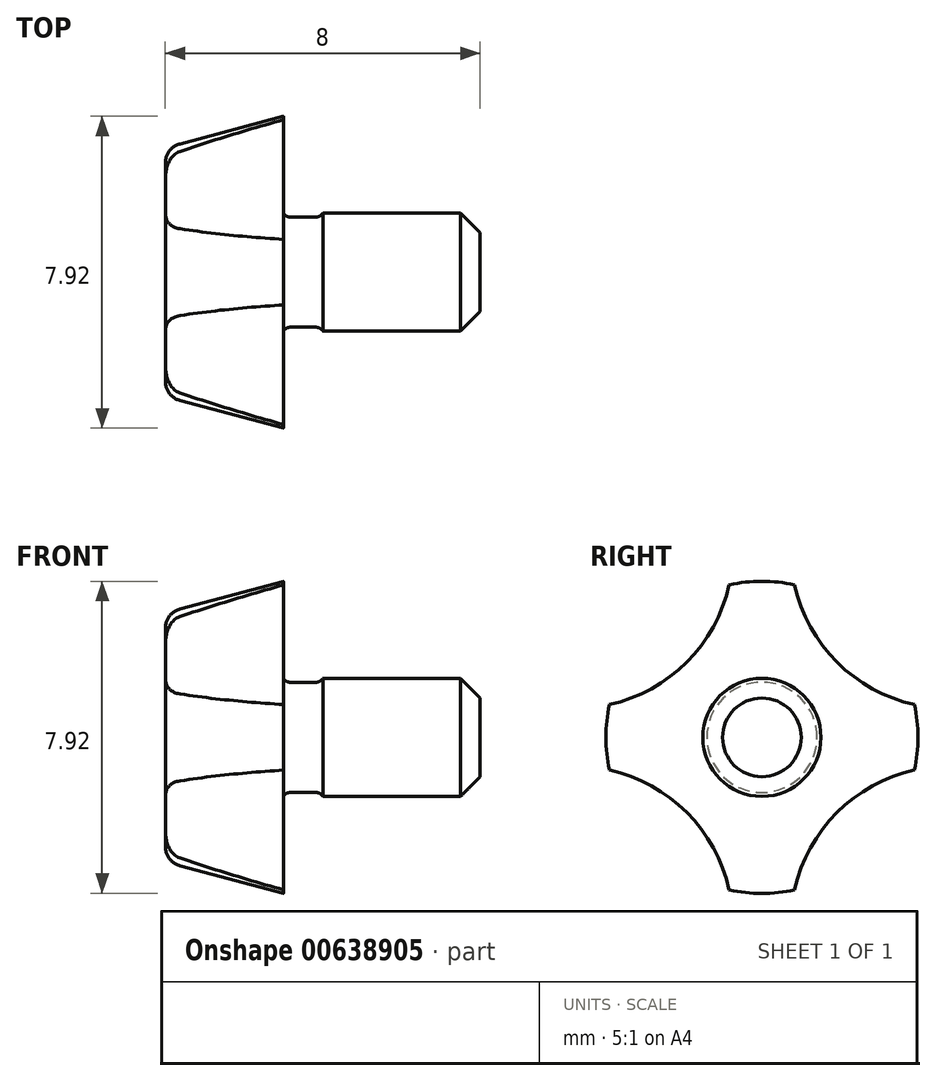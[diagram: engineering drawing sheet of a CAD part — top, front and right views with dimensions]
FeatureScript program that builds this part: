
annotation { "Feature Type Name" : "Feature", "Feature Type Description" : "" }
export const myFeature = defineFeature(function(context is Context, id is Id, definition is map)
    precondition{}
    {
        {
            var Q0;
            Q0=qCreatedBy(makeId("Front.planeOp"),FACE);
            var sketch = newSketch(context, id + "F0", { "sketchPlane" : qUnion([Q0])});
            skArc(sketch, "E0", {"start": v(6.56, 3.26) * mm, "mid": v(6.3, 3.08) * mm, "end": v(6.2, 2.78) * mm});
            skArc(sketch, "E1", {"start": v(6.2, -2.78) * mm, "mid": v(6.3, -3.08) * mm, "end": v(6.56, -3.26) * mm});
            skLineSegment(sketch, "E2", {"start": v(14.54, 0) * mm, "end": v(6.2, 0) * mm});
            skLineSegment(sketch, "E3", {"start": v(9.2, -3.96) * mm, "end": v(9.2, 3.96) * mm});
            skLineSegment(sketch, "E4", {"start": v(6.2, 2.78) * mm, "end": v(6.2, -2.78) * mm});
            skLineSegment(sketch, "E5", {"start": v(6.56, 3.26) * mm, "end": v(9.2, 3.96) * mm});
            skLineSegment(sketch, "E6", {"start": v(6.56, -3.26) * mm, "end": v(9.2, -3.96) * mm});
            skLineSegment(sketch, "E7", {"start": v(9.37, -1.4) * mm, "end": v(9.37, 1.4) * mm});
            skArc(sketch, "E8", {"start": v(9.37, -1.4) * mm, "mid": v(9.27, -1.43) * mm, "end": v(9.2, -1.5) * mm});
            skArc(sketch, "E9", {"start": v(9.2, 1.5) * mm, "mid": v(9.27, 1.43) * mm, "end": v(9.37, 1.4) * mm});
            skLineSegment(sketch, "E10", {"start": v(13.7, -1.5) * mm, "end": v(13.7, 1.5) * mm});
            skLineSegment(sketch, "E11", {"start": v(10.2, -1.5) * mm, "end": v(10.2, 1.5) * mm});
            skLineSegment(sketch, "E12", {"start": v(10.2, -1.5) * mm, "end": v(13.7, -1.5) * mm});
            skLineSegment(sketch, "E13", {"start": v(13.7, 1.5) * mm, "end": v(10.2, 1.5) * mm});
            skLineSegment(sketch, "E14", {"start": v(14.2, -1) * mm, "end": v(14.2, 1) * mm});
            skLineSegment(sketch, "E15", {"start": v(13.7, -1.5) * mm, "end": v(14.2, -1) * mm});
            skLineSegment(sketch, "E16", {"start": v(14.2, 1) * mm, "end": v(13.7, 1.5) * mm});
            skLineSegment(sketch, "E17", {"start": v(10.02, -1.4) * mm, "end": v(10.02, 1.4) * mm});
            skArc(sketch, "E18", {"start": v(10.2, -1.5) * mm, "mid": v(10.12, -1.43) * mm, "end": v(10.02, -1.4) * mm});
            skArc(sketch, "E19", {"start": v(10.02, 1.4) * mm, "mid": v(10.12, 1.43) * mm, "end": v(10.2, 1.5) * mm});
            skLineSegment(sketch, "E20", {"start": v(9.37, -1.4) * mm, "end": v(10.02, -1.4) * mm});
            skLineSegment(sketch, "E21", {"start": v(10.02, 1.4) * mm, "end": v(9.37, 1.4) * mm});
            skCircle(sketch, "E22", {"center": v(-10.58, 0) * mm, "radius": 1.5 * mm});
            skArc(sketch, "E23", {"start": v(-9.75, 3.88) * mm, "mid": v(-10.58, 3.96) * mm, "end": v(-11.41, 3.88) * mm});
            skArc(sketch, "E24", {"start": v(-6.7, -0.83) * mm, "mid": v(-6.62, 0) * mm, "end": v(-6.7, 0.83) * mm});
            skArc(sketch, "E25", {"start": v(-11.41, -3.88) * mm, "mid": v(-10.58, -3.96) * mm, "end": v(-9.75, -3.88) * mm});
            skArc(sketch, "E26", {"start": v(-14.46, 0.83) * mm, "mid": v(-14.54, 0) * mm, "end": v(-14.46, -0.83) * mm});
            skArc(sketch, "E27", {"start": v(-13.52, 1.17) * mm, "mid": v(-13.74, 0) * mm, "end": v(-13.52, -1.17) * mm});
            skArc(sketch, "E28", {"start": v(-11.75, -2.94) * mm, "mid": v(-10.58, -3.16) * mm, "end": v(-9.41, -2.94) * mm});
            skArc(sketch, "E29", {"start": v(-7.64, -1.17) * mm, "mid": v(-7.42, 0) * mm, "end": v(-7.64, 1.17) * mm});
            skArc(sketch, "E30", {"start": v(-9.41, 2.94) * mm, "mid": v(-10.58, 3.16) * mm, "end": v(-11.75, 2.94) * mm});
            skArc(sketch, "E31", {"start": v(-9.75, 3.88) * mm, "mid": v(-8.67, 1.91) * mm, "end": v(-6.7, 0.83) * mm});
            skArc(sketch, "E32", {"start": v(-6.7, -0.83) * mm, "mid": v(-8.67, -1.91) * mm, "end": v(-9.75, -3.88) * mm});
            skArc(sketch, "E33", {"start": v(-11.41, -3.88) * mm, "mid": v(-12.49, -1.91) * mm, "end": v(-14.46, -0.83) * mm});
            skArc(sketch, "E34", {"start": v(-14.46, 0.83) * mm, "mid": v(-12.49, 1.91) * mm, "end": v(-11.41, 3.88) * mm});
            skCircle(sketch, "E35", {"center": v(-10.58, 0) * mm, "radius": 3.96 * mm});
            skSolve(sketch);
        }
        {
            var Q0;
            {var subQ5=sQuery(id+"F0.wireOp",EDGE,"E9");Q0=makeQuery(id+"F0.imprint","IMPRINT",FACE,{"disambiguationData":[TD([[makeQuery(id+"F0.imprint","IMPRINT",EDGE,{"derivedFrom":subQ5}),-1.0]])]});}
            var Q1;
            {var subQ5=sQuery(id+"F0.wireOp",EDGE,"E21");Q1=makeQuery(id+"F0.imprint","IMPRINT",FACE,{"disambiguationData":[TD([[makeQuery(id+"F0.imprint","IMPRINT",EDGE,{"derivedFrom":subQ5}),1.0]])]});}
            var Q2;
            {var subQ5=sQuery(id+"F0.wireOp",EDGE,"E19");Q2=makeQuery(id+"F0.imprint","IMPRINT",FACE,{"disambiguationData":[TD([[makeQuery(id+"F0.imprint","IMPRINT",EDGE,{"derivedFrom":subQ5}),-1.0]])]});}
            var Q3;
            {var subQ5=sQuery(id+"F0.wireOp",EDGE,"E13");Q3=makeQuery(id+"F0.imprint","IMPRINT",FACE,{"disambiguationData":[TD([[makeQuery(id+"F0.imprint","IMPRINT",EDGE,{"derivedFrom":subQ5}),1.0]])]});}
            var Q4;
            {var subQ5=sQuery(id+"F0.wireOp",EDGE,"E16");Q4=makeQuery(id+"F0.imprint","IMPRINT",FACE,{"disambiguationData":[TD([[makeQuery(id+"F0.imprint","IMPRINT",EDGE,{"derivedFrom":subQ5}),1.0]])]});}
            var Q5;
            {var subQ3=sQuery(id+"F0.wireOp",EDGE,"E0");Q5=makeQuery(id+"F0.imprint","IMPRINT",FACE,{"disambiguationData":[TD([[makeQuery(id+"F0.imprint","IMPRINT",EDGE,{"derivedFrom":subQ3}),1.0]])]});}
            var Q6;
            Q6=sQuery(id+"F0.wireOp",EDGE,"E2");
            revolve(context, id + "F1", {"entities" : qUnion([Q0, Q1, Q2, Q3, Q4, Q5]), "axis" : qUnion([Q6]), "revolveType" : RevolveType.FULL});
        }
        {
            var Q0;
            Q0=makeQuery(id+"F1.opRevolve","SWEPT_FACE",FACE,{"disambiguationData":[OSD([sQuery(id+"F0.wireOp",EDGE,"E4")])]});
            var sketch = newSketch(context, id + "F2", { "sketchPlane" : qUnion([Q0])});
            skPoint(sketch, "E36", {"position": v(0, 0) * mm});
            skCircle(sketch, "E37", {"center": v(0, 0) * mm, "radius": 1.5 * mm});
            skArc(sketch, "E38", {"start": v(0.83, 3.88) * mm, "mid": v(0, 3.96) * mm, "end": v(-0.83, 3.88) * mm});
            skArc(sketch, "E39", {"start": v(3.88, -0.83) * mm, "mid": v(3.96, 0) * mm, "end": v(3.88, 0.83) * mm});
            skArc(sketch, "E40", {"start": v(-0.83, -3.88) * mm, "mid": v(0, -3.96) * mm, "end": v(0.83, -3.88) * mm});
            skArc(sketch, "E41", {"start": v(-3.88, 0.83) * mm, "mid": v(-3.96, 0) * mm, "end": v(-3.88, -0.83) * mm});
            skArc(sketch, "E42", {"start": v(-2.94, 1.17) * mm, "mid": v(-3.16, 0) * mm, "end": v(-2.94, -1.17) * mm});
            skArc(sketch, "E43", {"start": v(-1.17, -2.94) * mm, "mid": v(0, -3.16) * mm, "end": v(1.17, -2.94) * mm});
            skArc(sketch, "E44", {"start": v(2.94, -1.17) * mm, "mid": v(3.16, 0) * mm, "end": v(2.94, 1.17) * mm});
            skArc(sketch, "E45", {"start": v(1.17, 2.94) * mm, "mid": v(0, 3.16) * mm, "end": v(-1.17, 2.94) * mm});
            skArc(sketch, "E46", {"start": v(0.83, 3.88) * mm, "mid": v(1.91, 1.91) * mm, "end": v(3.88, 0.83) * mm});
            skArc(sketch, "E47", {"start": v(3.88, -0.83) * mm, "mid": v(1.91, -1.91) * mm, "end": v(0.83, -3.88) * mm});
            skArc(sketch, "E48", {"start": v(-0.83, -3.88) * mm, "mid": v(-1.91, -1.91) * mm, "end": v(-3.88, -0.83) * mm});
            skArc(sketch, "E49", {"start": v(-3.88, 0.83) * mm, "mid": v(-1.91, 1.91) * mm, "end": v(-0.83, 3.88) * mm});
            skCircle(sketch, "E50", {"center": v(0, 0) * mm, "radius": 3.96 * mm});
            skSolve(sketch);
        }
        {
            var Q0;
            {var subQ0=sQuery(id+"F2.wireOp",EDGE,"E47");var subQ8=makeQuery(id+"F2.imprint","INTERSECT",VERTEX,{"derivedFrom":[sQuery(id+"F2.wireOp",EDGE,"E43"),subQ0]});Q0=makeQuery(id+"F2.imprint","IMPRINT",FACE,{"disambiguationData":[TD([[makeQuery(id+"F2.imprint","IMPRINT",EDGE,{"disambiguationData":[TD([[subQ8,-1.0]])],"derivedFrom":subQ0}),1.0]])]});}
            var Q1;
            {var subQ0=sQuery(id+"F2.wireOp",EDGE,"E47");var subQ1=makeQuery(id+"F1.opRevolve","SWEPT_EDGE",EDGE,{"disambiguationData":[OSD([sQuery(id+"F0.wireOp",EDGE,"E0"),sQuery(id+"F0.wireOp",EDGE,"E4")])]});var subQ2=makeQuery(id+"F2.imprint","INTERSECT",VERTEX,{"disambiguationData":[OD(0.0)],"derivedFrom":[subQ1,subQ0]});Q1=makeQuery(id+"F2.imprint","IMPRINT",FACE,{"disambiguationData":[TD([[makeQuery(id+"F2.imprint","IMPRINT",EDGE,{"disambiguationData":[TD([[subQ2,-1.0]])],"derivedFrom":subQ0}),1.0]])]});}
            var Q2;
            {var subQ0=sQuery(id+"F2.wireOp",EDGE,"E48");var subQ4=makeQuery(id+"F2.imprint","INTERSECT",VERTEX,{"derivedFrom":[sQuery(id+"F2.wireOp",EDGE,"E42"),subQ0]});Q2=makeQuery(id+"F2.imprint","IMPRINT",FACE,{"disambiguationData":[TD([[makeQuery(id+"F2.imprint","IMPRINT",EDGE,{"disambiguationData":[TD([[subQ4,-1.0]])],"derivedFrom":subQ0}),1.0]])]});}
            var Q3;
            {var subQ0=sQuery(id+"F2.wireOp",EDGE,"E48");var subQ1=makeQuery(id+"F1.opRevolve","SWEPT_EDGE",EDGE,{"disambiguationData":[OSD([sQuery(id+"F0.wireOp",EDGE,"E0"),sQuery(id+"F0.wireOp",EDGE,"E4")])]});var subQ2=makeQuery(id+"F2.imprint","INTERSECT",VERTEX,{"disambiguationData":[OD(0.0)],"derivedFrom":[subQ1,subQ0]});Q3=makeQuery(id+"F2.imprint","IMPRINT",FACE,{"disambiguationData":[TD([[makeQuery(id+"F2.imprint","IMPRINT",EDGE,{"disambiguationData":[TD([[subQ2,-1.0]])],"derivedFrom":subQ0}),1.0]])]});}
            var Q4;
            {var subQ0=sQuery(id+"F2.wireOp",EDGE,"E49");var subQ1=makeQuery(id+"F1.opRevolve","SWEPT_EDGE",EDGE,{"disambiguationData":[OSD([sQuery(id+"F0.wireOp",EDGE,"E0"),sQuery(id+"F0.wireOp",EDGE,"E4")])]});var subQ2=makeQuery(id+"F2.imprint","INTERSECT",VERTEX,{"disambiguationData":[OD(0.0)],"derivedFrom":[subQ1,subQ0]});Q4=makeQuery(id+"F2.imprint","IMPRINT",FACE,{"disambiguationData":[TD([[makeQuery(id+"F2.imprint","IMPRINT",EDGE,{"disambiguationData":[TD([[subQ2,-1.0]])],"derivedFrom":subQ0}),1.0]])]});}
            var Q5;
            {var subQ0=sQuery(id+"F2.wireOp",EDGE,"E49");var subQ4=makeQuery(id+"F2.imprint","INTERSECT",VERTEX,{"derivedFrom":[sQuery(id+"F2.wireOp",EDGE,"E45"),subQ0]});Q5=makeQuery(id+"F2.imprint","IMPRINT",FACE,{"disambiguationData":[TD([[makeQuery(id+"F2.imprint","IMPRINT",EDGE,{"disambiguationData":[TD([[subQ4,-1.0]])],"derivedFrom":subQ0}),1.0]])]});}
            var Q6;
            {var subQ0=sQuery(id+"F2.wireOp",EDGE,"E46");var subQ1=makeQuery(id+"F1.opRevolve","SWEPT_EDGE",EDGE,{"disambiguationData":[OSD([sQuery(id+"F0.wireOp",EDGE,"E0"),sQuery(id+"F0.wireOp",EDGE,"E4")])]});var subQ2=makeQuery(id+"F2.imprint","INTERSECT",VERTEX,{"disambiguationData":[OD(0.0)],"derivedFrom":[subQ1,subQ0]});Q6=makeQuery(id+"F2.imprint","IMPRINT",FACE,{"disambiguationData":[TD([[makeQuery(id+"F2.imprint","IMPRINT",EDGE,{"disambiguationData":[TD([[subQ2,-1.0]])],"derivedFrom":subQ0}),1.0]])]});}
            var Q7;
            {var subQ0=sQuery(id+"F2.wireOp",EDGE,"E46");var subQ7=makeQuery(id+"F2.imprint","INTERSECT",VERTEX,{"derivedFrom":[sQuery(id+"F2.wireOp",EDGE,"E45"),subQ0]});Q7=makeQuery(id+"F2.imprint","IMPRINT",FACE,{"disambiguationData":[TD([[makeQuery(id+"F2.imprint","IMPRINT",EDGE,{"disambiguationData":[TD([[subQ7,1.0]])],"derivedFrom":subQ0}),1.0]])]});}
            extrude(context, id + "F3", {"entities" : qUnion([Q0, Q1, Q2, Q3, Q4, Q5, Q6, Q7]), "operationType" : NewBodyOperationType.REMOVE, "oppositeDirection" : true, "depth" : 25 * mm, "offsetDistance" : 25 * mm});
        }
    });
